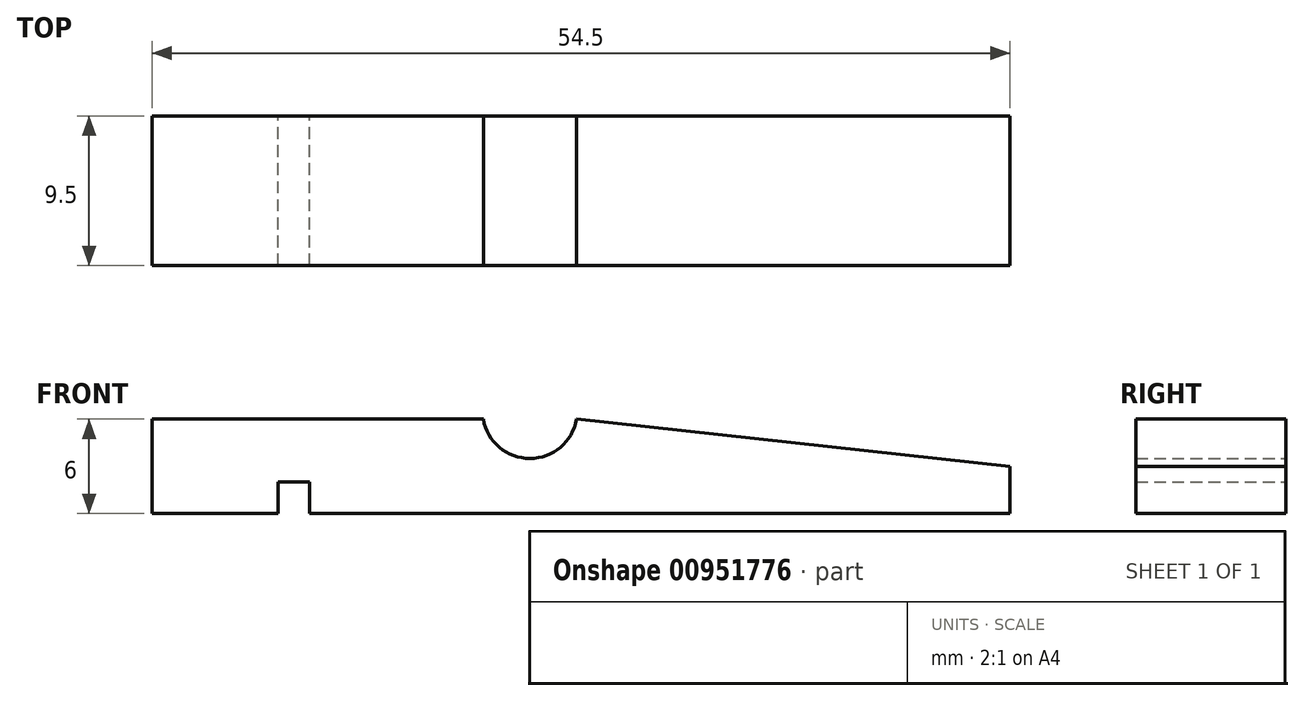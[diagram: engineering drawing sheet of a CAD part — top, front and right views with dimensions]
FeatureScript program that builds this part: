
annotation { "Feature Type Name" : "Feature", "Feature Type Description" : "" }
export const myFeature = defineFeature(function(context is Context, id is Id, definition is map)
    precondition{}
    {
        {
            var Q0;
            Q0=qCreatedBy(makeId("Front.planeOp"),FACE);
            var sketch = newSketch(context, id + "F0", { "sketchPlane" : qUnion([Q0])});
            skLineSegment(sketch, "E0.right", {"start": v(30.5, -6.5) * mm, "end": v(30.5, -3.5) * mm});
            skLineSegment(sketch, "E1", {"start": v(2.96, -0.5) * mm, "end": v(30.5, -3.5) * mm});
            skLineSegment(sketch, "E2.trimOffspring", {"start": v(-24, -0.5) * mm, "end": v(-2.96, -0.5) * mm});
            skPoint(sketch, "E3.center.orphan", {"position": v(0, 0) * mm});
            skArc(sketch, "E4", {"start": v(-2.96, -0.5) * mm, "mid": v(0, -3) * mm, "end": v(2.96, -0.5) * mm});
            skLineSegment(sketch, "E5.top", {"start": v(-16, -4.5) * mm, "end": v(-14, -4.5) * mm});
            skLineSegment(sketch, "E5.left", {"start": v(-16, -6.5) * mm, "end": v(-16, -4.5) * mm});
            skLineSegment(sketch, "E5.right", {"start": v(-14, -6.5) * mm, "end": v(-14, -4.5) * mm});
            skLineSegment(sketch, "E6.trimOffspring", {"start": v(-14, -6.5) * mm, "end": v(30.5, -6.5) * mm});
            skPoint(sketch, "E7", {"position": v(-15, -4.5) * mm});
            skLineSegment(sketch, "E8", {"start": v(-24, -0.5) * mm, "end": v(-24, -6.5) * mm});
            skLineSegment(sketch, "E9", {"start": v(-24, -6.5) * mm, "end": v(-16, -6.5) * mm});
            skLineSegment(sketch, "E10", {"start": v(-2.96, -0.5) * mm, "end": v(2.96, -0.5) * mm, "construction": true});
            skSolve(sketch);
        }
        {
            var Q0;
            Q0=makeQuery(id+"F0.imprint","IMPRINT",FACE,{"disambiguationData":[TD([[makeQuery(id+"F0.imprint","IMPRINT",EDGE,{"derivedFrom":sQuery(id+"F0.wireOp",EDGE,"E0.right")}),1.0]])]});
            extrude(context, id + "F1", {"entities" : qUnion([Q0]), "offsetDistance" : 25 * mm, "depth" : 9.5 * mm});
        }
    });
